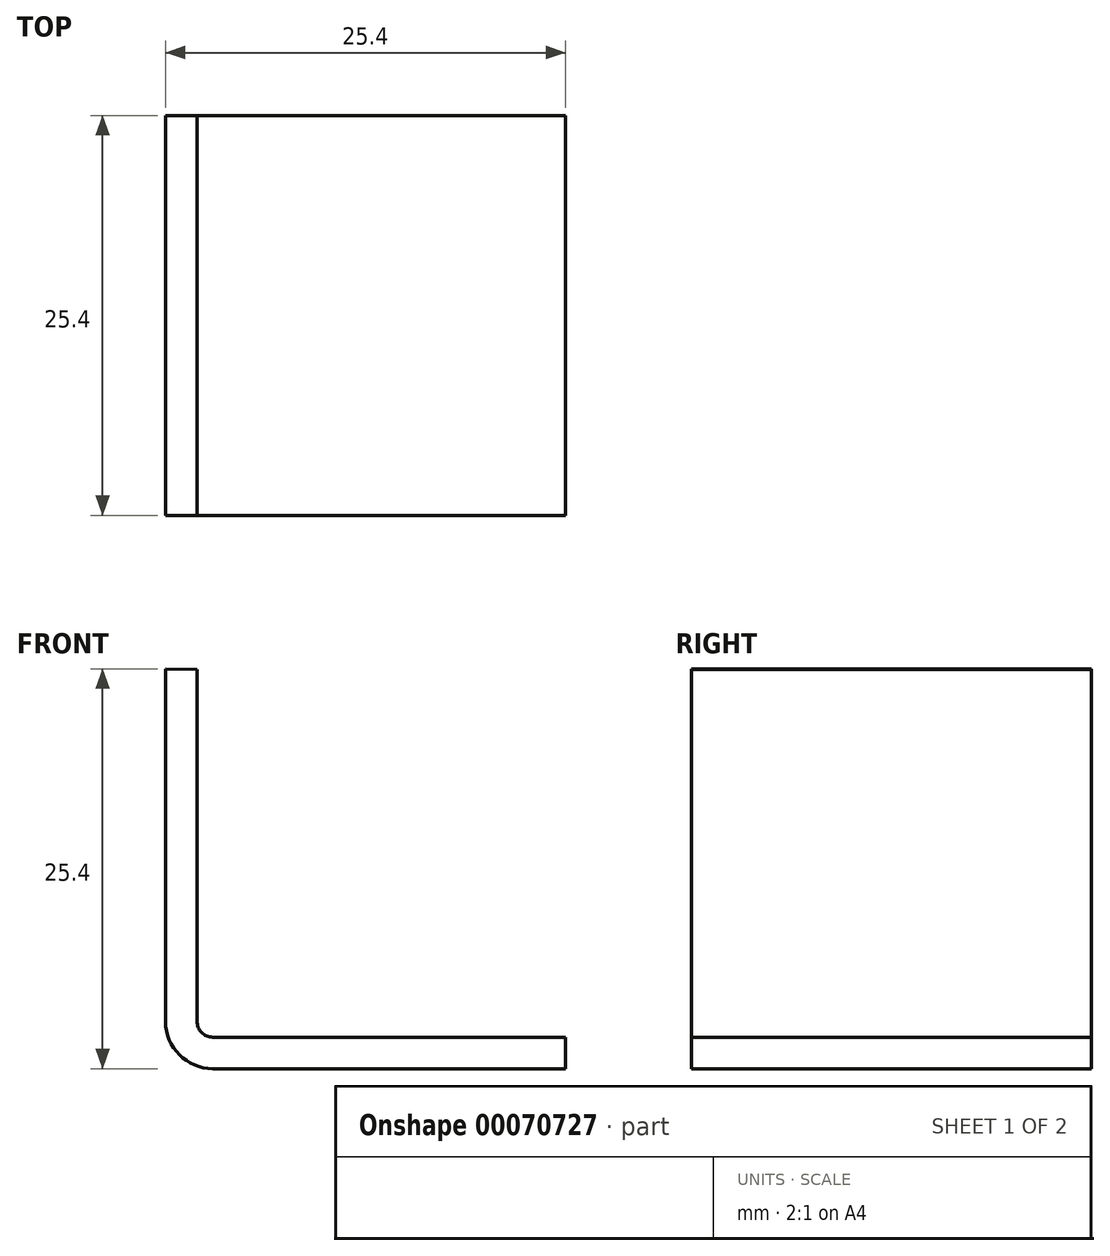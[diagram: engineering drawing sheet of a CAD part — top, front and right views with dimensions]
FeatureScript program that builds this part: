
annotation { "Feature Type Name" : "Feature", "Feature Type Description" : "" }
export const myFeature = defineFeature(function(context is Context, id is Id, definition is map)
    precondition{}
    {
        {
            var Q0;
            Q0=qCreatedBy(makeId("Front.planeOp"),FACE);
            var sketch = newSketch(context, id + "F0", { "sketchPlane" : qUnion([Q0])});
            skLineSegment(sketch, "E0", {"start": v(0, 3) * mm, "end": v(0, 25.4) * mm});
            skLineSegment(sketch, "E1", {"start": v(0, 25.4) * mm, "end": v(2, 25.35) * mm});
            skLineSegment(sketch, "E2", {"start": v(2, 25.35) * mm, "end": v(2, 3) * mm});
            skLineSegment(sketch, "E3", {"start": v(3, 2) * mm, "end": v(25.4, 2) * mm});
            skLineSegment(sketch, "E4", {"start": v(25.4, 2) * mm, "end": v(25.4, 0) * mm});
            skLineSegment(sketch, "E5", {"start": v(25.4, 0) * mm, "end": v(3, 0) * mm});
            skPoint(sketch, "E6.visualSharp", {"position": v(2, 2) * mm});
            skArc(sketch, "E6.filletArc", {"start": v(2, 3) * mm, "mid": v(2.3, 2.3) * mm, "end": v(3, 2) * mm});
            skPoint(sketch, "E7.visualSharp", {"position": v(0, 0) * mm});
            skArc(sketch, "E7.filletArc", {"start": v(0, 3) * mm, "mid": v(0.88, 0.88) * mm, "end": v(3, 0) * mm});
            skSolve(sketch);
        }
        {
            var Q0;
            Q0 = qSketchRegion(id + "F0", true);
            extrude(context, id + "F1", {"entities" : qUnion([Q0]), "depth" : 25.4 * mm});
        }
    });
